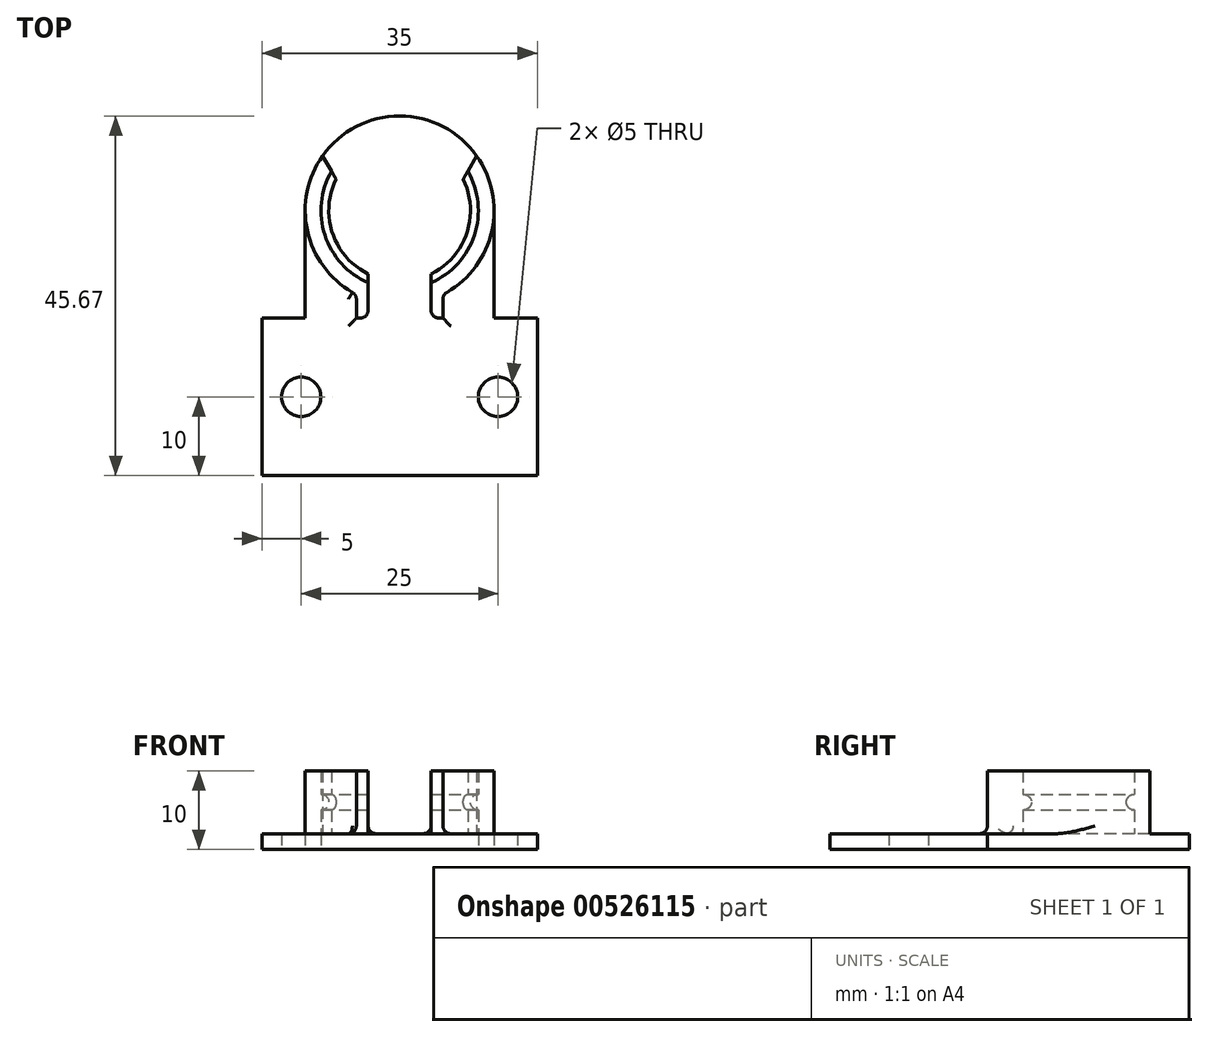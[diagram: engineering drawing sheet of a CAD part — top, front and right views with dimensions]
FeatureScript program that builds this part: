
annotation { "Feature Type Name" : "Feature", "Feature Type Description" : "" }
export const myFeature = defineFeature(function(context is Context, id is Id, definition is map)
    precondition{}
    {
        {
            var Q0;
            Q0=qCreatedBy(makeId("Top.planeOp"),FACE);
            var sketch = newSketch(context, id + "F0", { "sketchPlane" : qUnion([Q0])});
            skArc(sketch, "E0", {"start": v(-5.5, 1.5) * mm, "mid": v(0, 24.17) * mm, "end": v(5.5, 1.5) * mm});
            skArc(sketch, "E1", {"start": v(-5.5, -1.5) * mm, "mid": v(0, -24.17) * mm, "end": v(5.5, -1.5) * mm});
            skLineSegment(sketch, "E2", {"start": v(-5.5, 1.5) * mm, "end": v(-5.5, -1.5) * mm});
            skLineSegment(sketch, "E3", {"start": v(5.5, 1.5) * mm, "end": v(5.5, -1.5) * mm});
            skSolve(sketch);
        }
        {
            var Q0;
            Q0=qSketchRegion(id+"F0",true);
            extrude(context, id + "F1", {"entities" : qUnion([Q0]), "depth" : 2 * mm, "offsetDistance" : 25 * mm});
        }
        {
            var Q0;
            Q0=makeQuery(id+"F1.opExtrude","CAP_FACE",FACE,{"disambiguationData":[OSD([sQuery(id+"F0.wireOp",EDGE,"E0"),sQuery(id+"F0.wireOp",EDGE,"E1"),sQuery(id+"F0.wireOp",EDGE,"E2"),sQuery(id+"F0.wireOp",EDGE,"E3")])],"isStart":false});
            var sketch = newSketch(context, id + "F2", { "sketchPlane" : qUnion([Q0])});
            skArc(sketch, "E4", {"start": v(8.66, 17.17) * mm, "mid": v(9.5, 9.04) * mm, "end": v(4, 3) * mm});
            skArc(sketch, "E5", {"start": v(9.78, 19.11) * mm, "mid": v(11.66, 9.33) * mm, "end": v(5.5, 1.5) * mm});
            skArc(sketch, "E6", {"start": v(-8.66, 17.17) * mm, "mid": v(-9.5, 9.04) * mm, "end": v(-4, 3) * mm});
            skArc(sketch, "E7", {"start": v(5.5, -3.81) * mm, "mid": v(9.59, -9.32) * mm, "end": v(9.17, -16.17) * mm});
            skLineSegment(sketch, "E8", {"start": v(9.78, 19.11) * mm, "end": v(8.66, 17.17) * mm});
            skLineSegment(sketch, "E9", {"start": v(-8.66, 17.17) * mm, "end": v(-9.78, 19.11) * mm});
            skLineSegment(sketch, "E10", {"start": v(5.5, 1.5) * mm, "end": v(5.5, -3.81) * mm});
            skLineSegment(sketch, "E11", {"start": v(-4, 3) * mm, "end": v(-4, -6.24) * mm});
            skLineSegment(sketch, "E12", {"start": v(-4, -6.24) * mm, "end": v(-9.17, -16.17) * mm});
            skLineSegment(sketch, "E13", {"start": v(9.17, -16.17) * mm, "end": v(4, -6.24) * mm});
            skLineSegment(sketch, "E14", {"start": v(4, -6.24) * mm, "end": v(4, 3) * mm});
            skArc(sketch, "E15", {"start": v(-9.78, 19.11) * mm, "mid": v(-11.66, 9.33) * mm, "end": v(-5.5, 1.5) * mm});
            skArc(sketch, "E16", {"start": v(-9.17, -16.17) * mm, "mid": v(-9.59, -9.32) * mm, "end": v(-5.5, -3.81) * mm});
            skLineSegment(sketch, "E17", {"start": v(-5.5, 1.5) * mm, "end": v(-5.5, -3.81) * mm});
            skArc(sketch, "E18.0", {"start": v(-5.5, 1.5) * mm, "mid": v(0, 24.17) * mm, "end": v(5.5, 1.5) * mm, "construction": true});
            skArc(sketch, "E19.0", {"start": v(-5.5, -1.5) * mm, "mid": v(0, -24.17) * mm, "end": v(5.5, -1.5) * mm, "construction": true});
            skSolve(sketch);
        }
        {
            var Q0;
            Q0=qSketchRegion(id+"F2",true);
            extrude(context, id + "F3", {"entities" : qUnion([Q0]), "operationType" : NewBodyOperationType.ADD, "depth" : 3 * mm, "offsetDistance" : 25 * mm});
        }
        {
            var Q0;
            Q0=makeQuery(id+"F3.opExtrude","CAP_FACE",FACE,{"disambiguationData":[OSD([sQuery(id+"F2.wireOp",EDGE,"E4"),sQuery(id+"F2.wireOp",EDGE,"E5"),sQuery(id+"F2.wireOp",EDGE,"E7"),sQuery(id+"F2.wireOp",EDGE,"E8"),sQuery(id+"F2.wireOp",EDGE,"E10"),sQuery(id+"F2.wireOp",EDGE,"E13"),sQuery(id+"F2.wireOp",EDGE,"E14")])],"isStart":false});
            var sketch = newSketch(context, id + "F4", { "sketchPlane" : qUnion([Q0])});
            skArc(sketch, "E20", {"start": v(-9.78, 19.11) * mm, "mid": v(-11.66, 9.33) * mm, "end": v(-5.5, 1.5) * mm});
            skArc(sketch, "E21", {"start": v(9.78, 19.11) * mm, "mid": v(11.66, 9.33) * mm, "end": v(5.5, 1.5) * mm});
            skArc(sketch, "E22", {"start": v(8.07, 16.15) * mm, "mid": v(8.53, 9.28) * mm, "end": v(4, 4.1) * mm});
            skArc(sketch, "E23", {"start": v(-8.07, 16.15) * mm, "mid": v(-8.53, 9.28) * mm, "end": v(-4, 4.1) * mm});
            skArc(sketch, "E24", {"start": v(5.5, -5.04) * mm, "mid": v(8.6, -9.53) * mm, "end": v(8.55, -14.98) * mm});
            skArc(sketch, "E25", {"start": v(-5.5, -5.04) * mm, "mid": v(-8.6, -9.53) * mm, "end": v(-8.55, -14.98) * mm});
            skLineSegment(sketch, "E26", {"start": v(-5.5, 1.5) * mm, "end": v(-5.5, -5.04) * mm});
            skLineSegment(sketch, "E27", {"start": v(5.5, 1.5) * mm, "end": v(5.5, -5.04) * mm});
            skLineSegment(sketch, "E28", {"start": v(-4, 4.1) * mm, "end": v(-4, -6.24) * mm});
            skLineSegment(sketch, "E29", {"start": v(-4, -6.24) * mm, "end": v(-8.55, -14.98) * mm});
            skLineSegment(sketch, "E30", {"start": v(4, 4.1) * mm, "end": v(4, -6.24) * mm});
            skLineSegment(sketch, "E31", {"start": v(4, -6.24) * mm, "end": v(8.55, -14.98) * mm});
            skLineSegment(sketch, "E32", {"start": v(8.07, 16.15) * mm, "end": v(9.78, 19.11) * mm});
            skLineSegment(sketch, "E33", {"start": v(-9.78, 19.11) * mm, "end": v(-8.07, 16.15) * mm});
            skLineSegment(sketch, "E34.0", {"start": v(-8.66, 17.17) * mm, "end": v(-9.78, 19.11) * mm, "construction": true});
            skLineSegment(sketch, "E35.0", {"start": v(9.78, 19.11) * mm, "end": v(8.66, 17.17) * mm, "construction": true});
            skLineSegment(sketch, "E36.0", {"start": v(-4, -6.24) * mm, "end": v(-9.17, -16.17) * mm, "construction": true});
            skLineSegment(sketch, "E37.0", {"start": v(9.17, -16.17) * mm, "end": v(4, -6.24) * mm, "construction": true});
            skArc(sketch, "E38.0", {"start": v(-9.78, 19.11) * mm, "mid": v(0, 24.17) * mm, "end": v(9.78, 19.11) * mm, "construction": true});
            skArc(sketch, "E39.0", {"start": v(-5.5, -1.5) * mm, "mid": v(0, -24.17) * mm, "end": v(5.5, -1.5) * mm, "construction": true});
            skSolve(sketch);
        }
        {
            var Q0;
            Q0=qSketchRegion(id+"F4",true);
            extrude(context, id + "F5", {"entities" : qUnion([Q0]), "operationType" : NewBodyOperationType.ADD, "depth" : 2 * mm, "offsetDistance" : 25 * mm});
        }
        {
            var Q0;
            Q0=makeQuery(id+"F5.opExtrude","CAP_FACE",FACE,{"disambiguationData":[OSD([sQuery(id+"F4.wireOp",EDGE,"E21"),sQuery(id+"F4.wireOp",EDGE,"E22"),sQuery(id+"F4.wireOp",EDGE,"E24"),sQuery(id+"F4.wireOp",EDGE,"E27"),sQuery(id+"F4.wireOp",EDGE,"E30"),sQuery(id+"F4.wireOp",EDGE,"E31"),sQuery(id+"F4.wireOp",EDGE,"E32")])],"isStart":false});
            var sketch = newSketch(context, id + "F6", { "sketchPlane" : qUnion([Q0])});
            skArc(sketch, "E40", {"start": v(8.66, 17.17) * mm, "mid": v(9.5, 9.04) * mm, "end": v(4, 3) * mm});
            skArc(sketch, "E41", {"start": v(9.78, 19.11) * mm, "mid": v(11.66, 9.33) * mm, "end": v(5.5, 1.5) * mm});
            skArc(sketch, "E42", {"start": v(-8.66, 17.17) * mm, "mid": v(-9.5, 9.04) * mm, "end": v(-4, 3) * mm});
            skArc(sketch, "E43", {"start": v(5.5, -3.81) * mm, "mid": v(9.59, -9.32) * mm, "end": v(9.17, -16.17) * mm});
            skLineSegment(sketch, "E44", {"start": v(9.78, 19.11) * mm, "end": v(8.66, 17.17) * mm});
            skLineSegment(sketch, "E45", {"start": v(-8.66, 17.17) * mm, "end": v(-9.78, 19.11) * mm});
            skLineSegment(sketch, "E46", {"start": v(5.5, 1.5) * mm, "end": v(5.5, -3.81) * mm});
            skLineSegment(sketch, "E47", {"start": v(-4, 3) * mm, "end": v(-4, -6.24) * mm});
            skLineSegment(sketch, "E48", {"start": v(-4, -6.24) * mm, "end": v(-9.17, -16.17) * mm});
            skLineSegment(sketch, "E49", {"start": v(9.17, -16.17) * mm, "end": v(4, -6.24) * mm});
            skLineSegment(sketch, "E50", {"start": v(4, -6.24) * mm, "end": v(4, 3) * mm});
            skArc(sketch, "E51", {"start": v(-9.78, 19.11) * mm, "mid": v(-11.66, 9.33) * mm, "end": v(-5.5, 1.5) * mm});
            skArc(sketch, "E52", {"start": v(-9.17, -16.17) * mm, "mid": v(-9.59, -9.32) * mm, "end": v(-5.5, -3.81) * mm});
            skLineSegment(sketch, "E53", {"start": v(-5.5, 1.5) * mm, "end": v(-5.5, -3.81) * mm});
            skArc(sketch, "E54.0", {"start": v(-5.5, -1.5) * mm, "mid": v(0, -24.17) * mm, "end": v(5.5, -1.5) * mm, "construction": true});
            skArc(sketch, "E55.0", {"start": v(-9.78, 19.11) * mm, "mid": v(0, 24.17) * mm, "end": v(9.78, 19.11) * mm, "construction": true});
            skSolve(sketch);
        }
        {
            var Q0;
            Q0=qSketchRegion(id+"F6",true);
            extrude(context, id + "F7", {"entities" : qUnion([Q0]), "operationType" : NewBodyOperationType.ADD, "depth" : 3 * mm, "offsetDistance" : 25 * mm});
        }
        {
            var Q0;
            Q0=makeQuery(id+"F5.opExtrude","CAP_EDGE",EDGE,{"disambiguationData":[OSD([sQuery(id+"F4.wireOp",EDGE,"E22")])],"isStart":false});
            var Q1;
            Q1=makeQuery(id+"F5.opExtrude","CAP_EDGE",EDGE,{"disambiguationData":[OSD([sQuery(id+"F4.wireOp",EDGE,"E23")])],"isStart":false});
            var Q2;
            Q2=makeQuery(id+"F5.opExtrude","CAP_EDGE",EDGE,{"disambiguationData":[OSD([sQuery(id+"F4.wireOp",EDGE,"E23")])],"isStart":true});
            var Q3;
            Q3=makeQuery(id+"F5.opExtrude","CAP_EDGE",EDGE,{"disambiguationData":[OSD([sQuery(id+"F4.wireOp",EDGE,"E22")])],"isStart":true});
            var Q4;
            Q4=makeQuery(id+"F5.opExtrude","CAP_EDGE",EDGE,{"disambiguationData":[OSD([sQuery(id+"F4.wireOp",EDGE,"E25")])],"isStart":true});
            var Q5;
            Q5=makeQuery(id+"F5.opExtrude","CAP_EDGE",EDGE,{"disambiguationData":[OSD([sQuery(id+"F4.wireOp",EDGE,"E25")])],"isStart":false});
            var Q6;
            Q6=makeQuery(id+"F5.opExtrude","CAP_EDGE",EDGE,{"disambiguationData":[OSD([sQuery(id+"F4.wireOp",EDGE,"E24")])],"isStart":false});
            var Q7;
            Q7=makeQuery(id+"F5.opExtrude","CAP_EDGE",EDGE,{"disambiguationData":[OSD([sQuery(id+"F4.wireOp",EDGE,"E24")])],"isStart":true});
            fillet(context, id + "F8", {"entities" : qUnion([Q0, Q1, Q2, Q3, Q4, Q5, Q6, Q7]), "radius" : 1 * mm, "tangentPropagation" : true, "allowEdgeOverflow" : false});
        }
        {
            var Q0;
            Q0=makeQuery(id+"F7.opExtrude","CAP_FACE",FACE,{"disambiguationData":[OSD([sQuery(id+"F6.wireOp",EDGE,"E40"),sQuery(id+"F6.wireOp",EDGE,"E41"),sQuery(id+"F6.wireOp",EDGE,"E43"),sQuery(id+"F6.wireOp",EDGE,"E44"),sQuery(id+"F6.wireOp",EDGE,"E46"),sQuery(id+"F6.wireOp",EDGE,"E49"),sQuery(id+"F6.wireOp",EDGE,"E50")])],"isStart":false});
            var sketch = newSketch(context, id + "F9", { "sketchPlane" : qUnion([Q0])});
            skLineSegment(sketch, "E56.bottom", {"start": v(-12, -1.5) * mm, "end": v(12, -1.5) * mm});
            skLineSegment(sketch, "E56.top", {"start": v(-12, -24.17) * mm, "end": v(12, -24.17) * mm});
            skLineSegment(sketch, "E56.left", {"start": v(-12, -1.5) * mm, "end": v(-12, -24.17) * mm});
            skLineSegment(sketch, "E56.right", {"start": v(12, -1.5) * mm, "end": v(12, -24.17) * mm});
            skSolve(sketch);
        }
        {
            var Q0;
            Q0 = qSketchRegion(id + "F9", true);
            extrude(context, id + "F10", {"entities" : qUnion([Q0]), "operationType" : NewBodyOperationType.REMOVE, "oppositeDirection" : true, "depth" : 10 * mm, "offsetDistance" : 25 * mm});
        }
        {
            var Q0;
            Q0=makeQuery(id+"F1.opExtrude","CAP_FACE",FACE,{"disambiguationData":[OSD([sQuery(id+"F0.wireOp",EDGE,"E0"),sQuery(id+"F0.wireOp",EDGE,"E1"),sQuery(id+"F0.wireOp",EDGE,"E2"),sQuery(id+"F0.wireOp",EDGE,"E3")])],"isStart":true});
            var sketch = newSketch(context, id + "F11", { "sketchPlane" : qUnion([Q0])});
            skLineSegment(sketch, "E57", {"start": v(12, -12.17) * mm, "end": v(-12, -12.17) * mm});
            skLineSegment(sketch, "E58", {"start": v(-12, -12.17) * mm, "end": v(-12, 1.5) * mm});
            skLineSegment(sketch, "E59", {"start": v(-12, 1.5) * mm, "end": v(-17.5, 1.5) * mm});
            skLineSegment(sketch, "E60", {"start": v(-17.5, 1.5) * mm, "end": v(-17.5, 21.5) * mm});
            skLineSegment(sketch, "E61", {"start": v(-17.5, 21.5) * mm, "end": v(17.5, 21.5) * mm});
            skLineSegment(sketch, "E62", {"start": v(17.5, 21.5) * mm, "end": v(17.5, 1.5) * mm});
            skLineSegment(sketch, "E63", {"start": v(17.5, 1.5) * mm, "end": v(12, 1.5) * mm});
            skLineSegment(sketch, "E64", {"start": v(12, 1.5) * mm, "end": v(12, -12.17) * mm});
            skCircle(sketch, "E65", {"center": v(-12.5, 11.5) * mm, "radius": 2.5 * mm});
            skCircle(sketch, "E66", {"center": v(12.5, 11.5) * mm, "radius": 2.5 * mm});
            skSolve(sketch);
        }
        {
            var Q0;
            Q0 = qSketchRegion(id + "F11", true);
            extrude(context, id + "F12", {"entities" : qUnion([Q0]), "operationType" : NewBodyOperationType.ADD, "oppositeDirection" : true, "depth" : 2 * mm, "offsetDistance" : 25 * mm});
        }
        {
            var Q0;
            Q0=makeQuery(id+"F3.opExtrude","CAP_EDGE",EDGE,{"disambiguationData":[OSD([sQuery(id+"F2.wireOp",EDGE,"E11")])],"isStart":true});
            var Q1;
            Q1=makeQuery(id+"F10.boolean.opBoolean","INTERSECT",EDGE,{"derivedFrom":[makeQuery(id+"F7.boolean.opBoolean","MERGE",FACE,{"derivedFrom":[makeQuery(id+"F5.boolean.opBoolean","MERGE",FACE,{"derivedFrom":[makeQuery(id+"F3.opExtrude","SWEPT_FACE",FACE,{"disambiguationData":[OSD([sQuery(id+"F2.wireOp",EDGE,"E11")])]}),makeQuery(id+"F5.opExtrude","SWEPT_FACE",FACE,{"disambiguationData":[OSD([sQuery(id+"F4.wireOp",EDGE,"E28")])]})]}),makeQuery(id+"F7.opExtrude","SWEPT_FACE",FACE,{"disambiguationData":[OSD([sQuery(id+"F6.wireOp",EDGE,"E47")])]})]}),makeQuery(id+"F10.opExtrude","SWEPT_FACE",FACE,{"disambiguationData":[OSD([sQuery(id+"F9.wireOp",EDGE,"E56.bottom")])]})]});
            var Q2;
            Q2=makeQuery(id+"F12.boolean.opBoolean","INTERSECT",EDGE,{"disambiguationData":[OD(0.0)],"derivedFrom":[makeQuery(id+"F7.boolean.opBoolean","MERGE",FACE,{"derivedFrom":[makeQuery(id+"F5.boolean.opBoolean","MERGE",FACE,{"derivedFrom":[makeQuery(id+"F3.boolean.opBoolean","MERGE",FACE,{"derivedFrom":[makeQuery(id+"F1.opExtrude","SWEPT_FACE",FACE,{"disambiguationData":[OSD([sQuery(id+"F0.wireOp",EDGE,"E0")])]}),makeQuery(id+"F3.opExtrude","SWEPT_FACE",FACE,{"disambiguationData":[OSD([sQuery(id+"F2.wireOp",EDGE,"E5")])]}),makeQuery(id+"F3.opExtrude","SWEPT_FACE",FACE,{"disambiguationData":[OSD([sQuery(id+"F2.wireOp",EDGE,"E15")])]})]}),makeQuery(id+"F5.opExtrude","SWEPT_FACE",FACE,{"disambiguationData":[OSD([sQuery(id+"F4.wireOp",EDGE,"E20")])]}),makeQuery(id+"F5.opExtrude","SWEPT_FACE",FACE,{"disambiguationData":[OSD([sQuery(id+"F4.wireOp",EDGE,"E21")])]})]}),makeQuery(id+"F7.opExtrude","SWEPT_FACE",FACE,{"disambiguationData":[OSD([sQuery(id+"F6.wireOp",EDGE,"E41")])]}),makeQuery(id+"F7.opExtrude","SWEPT_FACE",FACE,{"disambiguationData":[OSD([sQuery(id+"F6.wireOp",EDGE,"E51")])]})]}),makeQuery(id+"F12.opExtrude","CAP_FACE",FACE,{"disambiguationData":[OSD([sQuery(id+"F11.wireOp",EDGE,"E57"),sQuery(id+"F11.wireOp",EDGE,"E58"),sQuery(id+"F11.wireOp",EDGE,"E59"),sQuery(id+"F11.wireOp",EDGE,"E60"),sQuery(id+"F11.wireOp",EDGE,"E61"),sQuery(id+"F11.wireOp",EDGE,"E62"),sQuery(id+"F11.wireOp",EDGE,"E63"),sQuery(id+"F11.wireOp",EDGE,"E64"),sQuery(id+"F11.wireOp",EDGE,"E65"),sQuery(id+"F11.wireOp",EDGE,"E66")])],"isStart":false})]});
            var Q3;
            Q3=makeQuery(id+"F12.boolean.opBoolean","INTERSECT",EDGE,{"derivedFrom":[makeQuery(id+"F7.boolean.opBoolean","MERGE",FACE,{"derivedFrom":[makeQuery(id+"F5.boolean.opBoolean","MERGE",FACE,{"derivedFrom":[makeQuery(id+"F3.boolean.opBoolean","MERGE",FACE,{"derivedFrom":[makeQuery(id+"F1.opExtrude","SWEPT_FACE",FACE,{"disambiguationData":[OSD([sQuery(id+"F0.wireOp",EDGE,"E3")])]}),makeQuery(id+"F3.opExtrude","SWEPT_FACE",FACE,{"disambiguationData":[OSD([sQuery(id+"F2.wireOp",EDGE,"E10")])]})]}),makeQuery(id+"F5.opExtrude","SWEPT_FACE",FACE,{"disambiguationData":[OSD([sQuery(id+"F4.wireOp",EDGE,"E27")])]})]}),makeQuery(id+"F7.opExtrude","SWEPT_FACE",FACE,{"disambiguationData":[OSD([sQuery(id+"F6.wireOp",EDGE,"E46")])]})]}),makeQuery(id+"F12.opExtrude","CAP_FACE",FACE,{"disambiguationData":[OSD([sQuery(id+"F11.wireOp",EDGE,"E57"),sQuery(id+"F11.wireOp",EDGE,"E58"),sQuery(id+"F11.wireOp",EDGE,"E59"),sQuery(id+"F11.wireOp",EDGE,"E60"),sQuery(id+"F11.wireOp",EDGE,"E61"),sQuery(id+"F11.wireOp",EDGE,"E62"),sQuery(id+"F11.wireOp",EDGE,"E63"),sQuery(id+"F11.wireOp",EDGE,"E64"),sQuery(id+"F11.wireOp",EDGE,"E65"),sQuery(id+"F11.wireOp",EDGE,"E66")])],"isStart":false})]});
            var Q4;
            Q4=makeQuery(id+"F12.boolean.opBoolean","INTERSECT",EDGE,{"disambiguationData":[OD(1.0)],"derivedFrom":[makeQuery(id+"F10.boolean.opBoolean","COPY",FACE,{"derivedFrom":makeQuery(id+"F10.opExtrude","SWEPT_FACE",FACE,{"disambiguationData":[OSD([sQuery(id+"F9.wireOp",EDGE,"E56.bottom")])]})}),makeQuery(id+"F12.opExtrude","CAP_FACE",FACE,{"disambiguationData":[OSD([sQuery(id+"F11.wireOp",EDGE,"E57"),sQuery(id+"F11.wireOp",EDGE,"E58"),sQuery(id+"F11.wireOp",EDGE,"E59"),sQuery(id+"F11.wireOp",EDGE,"E60"),sQuery(id+"F11.wireOp",EDGE,"E61"),sQuery(id+"F11.wireOp",EDGE,"E62"),sQuery(id+"F11.wireOp",EDGE,"E63"),sQuery(id+"F11.wireOp",EDGE,"E64"),sQuery(id+"F11.wireOp",EDGE,"E65"),sQuery(id+"F11.wireOp",EDGE,"E66")])],"isStart":false})]});
            var Q5;
            Q5=makeQuery(id+"F10.boolean.opBoolean","INTERSECT",EDGE,{"derivedFrom":[makeQuery(id+"F7.boolean.opBoolean","MERGE",FACE,{"derivedFrom":[makeQuery(id+"F5.boolean.opBoolean","MERGE",FACE,{"derivedFrom":[makeQuery(id+"F3.opExtrude","SWEPT_FACE",FACE,{"disambiguationData":[OSD([sQuery(id+"F2.wireOp",EDGE,"E14")])]}),makeQuery(id+"F5.opExtrude","SWEPT_FACE",FACE,{"disambiguationData":[OSD([sQuery(id+"F4.wireOp",EDGE,"E30")])]})]}),makeQuery(id+"F7.opExtrude","SWEPT_FACE",FACE,{"disambiguationData":[OSD([sQuery(id+"F6.wireOp",EDGE,"E50")])]})]}),makeQuery(id+"F10.opExtrude","SWEPT_FACE",FACE,{"disambiguationData":[OSD([sQuery(id+"F9.wireOp",EDGE,"E56.bottom")])]})]});
            var Q6;
            Q6=makeQuery(id+"F12.boolean.opBoolean","INTERSECT",EDGE,{"disambiguationData":[OD(1.0)],"derivedFrom":[makeQuery(id+"F7.boolean.opBoolean","MERGE",FACE,{"derivedFrom":[makeQuery(id+"F5.boolean.opBoolean","MERGE",FACE,{"derivedFrom":[makeQuery(id+"F3.boolean.opBoolean","MERGE",FACE,{"derivedFrom":[makeQuery(id+"F1.opExtrude","SWEPT_FACE",FACE,{"disambiguationData":[OSD([sQuery(id+"F0.wireOp",EDGE,"E0")])]}),makeQuery(id+"F3.opExtrude","SWEPT_FACE",FACE,{"disambiguationData":[OSD([sQuery(id+"F2.wireOp",EDGE,"E5")])]}),makeQuery(id+"F3.opExtrude","SWEPT_FACE",FACE,{"disambiguationData":[OSD([sQuery(id+"F2.wireOp",EDGE,"E15")])]})]}),makeQuery(id+"F5.opExtrude","SWEPT_FACE",FACE,{"disambiguationData":[OSD([sQuery(id+"F4.wireOp",EDGE,"E20")])]}),makeQuery(id+"F5.opExtrude","SWEPT_FACE",FACE,{"disambiguationData":[OSD([sQuery(id+"F4.wireOp",EDGE,"E21")])]})]}),makeQuery(id+"F7.opExtrude","SWEPT_FACE",FACE,{"disambiguationData":[OSD([sQuery(id+"F6.wireOp",EDGE,"E41")])]}),makeQuery(id+"F7.opExtrude","SWEPT_FACE",FACE,{"disambiguationData":[OSD([sQuery(id+"F6.wireOp",EDGE,"E51")])]})]}),makeQuery(id+"F12.opExtrude","CAP_FACE",FACE,{"disambiguationData":[OSD([sQuery(id+"F11.wireOp",EDGE,"E57"),sQuery(id+"F11.wireOp",EDGE,"E58"),sQuery(id+"F11.wireOp",EDGE,"E59"),sQuery(id+"F11.wireOp",EDGE,"E60"),sQuery(id+"F11.wireOp",EDGE,"E61"),sQuery(id+"F11.wireOp",EDGE,"E62"),sQuery(id+"F11.wireOp",EDGE,"E63"),sQuery(id+"F11.wireOp",EDGE,"E64"),sQuery(id+"F11.wireOp",EDGE,"E65"),sQuery(id+"F11.wireOp",EDGE,"E66")])],"isStart":false})]});
            var Q7;
            Q7=makeQuery(id+"F12.boolean.opBoolean","INTERSECT",EDGE,{"derivedFrom":[makeQuery(id+"F7.boolean.opBoolean","MERGE",FACE,{"derivedFrom":[makeQuery(id+"F5.boolean.opBoolean","MERGE",FACE,{"derivedFrom":[makeQuery(id+"F3.boolean.opBoolean","MERGE",FACE,{"derivedFrom":[makeQuery(id+"F1.opExtrude","SWEPT_FACE",FACE,{"disambiguationData":[OSD([sQuery(id+"F0.wireOp",EDGE,"E2")])]}),makeQuery(id+"F3.opExtrude","SWEPT_FACE",FACE,{"disambiguationData":[OSD([sQuery(id+"F2.wireOp",EDGE,"E17")])]})]}),makeQuery(id+"F5.opExtrude","SWEPT_FACE",FACE,{"disambiguationData":[OSD([sQuery(id+"F4.wireOp",EDGE,"E26")])]})]}),makeQuery(id+"F7.opExtrude","SWEPT_FACE",FACE,{"disambiguationData":[OSD([sQuery(id+"F6.wireOp",EDGE,"E53")])]})]}),makeQuery(id+"F12.opExtrude","CAP_FACE",FACE,{"disambiguationData":[OSD([sQuery(id+"F11.wireOp",EDGE,"E57"),sQuery(id+"F11.wireOp",EDGE,"E58"),sQuery(id+"F11.wireOp",EDGE,"E59"),sQuery(id+"F11.wireOp",EDGE,"E60"),sQuery(id+"F11.wireOp",EDGE,"E61"),sQuery(id+"F11.wireOp",EDGE,"E62"),sQuery(id+"F11.wireOp",EDGE,"E63"),sQuery(id+"F11.wireOp",EDGE,"E64"),sQuery(id+"F11.wireOp",EDGE,"E65"),sQuery(id+"F11.wireOp",EDGE,"E66")])],"isStart":false})]});
            var Q8;
            Q8=makeQuery(id+"F7.boolean.opBoolean","MERGE",EDGE,{"derivedFrom":[makeQuery(id+"F5.boolean.opBoolean","MERGE",EDGE,{"derivedFrom":[makeQuery(id+"F3.boolean.opBoolean","MERGE",EDGE,{"derivedFrom":[makeQuery(id+"F1.opExtrude","SWEPT_EDGE",EDGE,{"disambiguationData":[OSD([sQuery(id+"F0.wireOp",EDGE,"E0"),sQuery(id+"F0.wireOp",EDGE,"E3")])]}),makeQuery(id+"F3.opExtrude","SWEPT_EDGE",EDGE,{"disambiguationData":[OSD([sQuery(id+"F2.wireOp",EDGE,"E5"),sQuery(id+"F2.wireOp",EDGE,"E10")])]})]}),makeQuery(id+"F5.opExtrude","SWEPT_EDGE",EDGE,{"disambiguationData":[OSD([sQuery(id+"F4.wireOp",EDGE,"E21"),sQuery(id+"F4.wireOp",EDGE,"E27")])]})]}),makeQuery(id+"F7.opExtrude","SWEPT_EDGE",EDGE,{"disambiguationData":[OSD([sQuery(id+"F6.wireOp",EDGE,"E41"),sQuery(id+"F6.wireOp",EDGE,"E46")])]})]});
            var Q9;
            Q9=makeQuery(id+"F7.boolean.opBoolean","MERGE",EDGE,{"derivedFrom":[makeQuery(id+"F5.boolean.opBoolean","MERGE",EDGE,{"derivedFrom":[makeQuery(id+"F3.boolean.opBoolean","MERGE",EDGE,{"derivedFrom":[makeQuery(id+"F1.opExtrude","SWEPT_EDGE",EDGE,{"disambiguationData":[OSD([sQuery(id+"F0.wireOp",EDGE,"E0"),sQuery(id+"F0.wireOp",EDGE,"E2")])]}),makeQuery(id+"F3.opExtrude","SWEPT_EDGE",EDGE,{"disambiguationData":[OSD([sQuery(id+"F2.wireOp",EDGE,"E15"),sQuery(id+"F2.wireOp",EDGE,"E17")])]})]}),makeQuery(id+"F5.opExtrude","SWEPT_EDGE",EDGE,{"disambiguationData":[OSD([sQuery(id+"F4.wireOp",EDGE,"E20"),sQuery(id+"F4.wireOp",EDGE,"E26")])]})]}),makeQuery(id+"F7.opExtrude","SWEPT_EDGE",EDGE,{"disambiguationData":[OSD([sQuery(id+"F6.wireOp",EDGE,"E51"),sQuery(id+"F6.wireOp",EDGE,"E53")])]})]});
            fillet(context, id + "F13", {"entities" : qUnion([Q0, Q1, Q2, Q3, Q4, Q5, Q6, Q7, Q8, Q9]), "radius" : 1 * mm, "tangentPropagation" : true, "allowEdgeOverflow" : false});
        }
    });
